# Revit family: 11
name_source: partatom
category: Lighting Fixtures
revit_build: Autodesk Revit 2014 (Build: 20130308_1515(x64)
units: mm (PartAtom-declared; Revit-internal decimal feet)

## types (1)
- P500324-104
    Apparent Load = 60 VA
    Assembly Code = D5020200
    Color Filter = 16777215
    Connector Description = Lighting Connector
    Default Elevation = 48 "
    Description = Embrace stylish simplicity with the Hinton Collection 1-Light Polished Nickel Clear Seeded Glass Vintage Hanging Pendant Light. The circular ceiling plate and industrial light base are coated in a crisp polished chrome finish. A light source glows from inside a clear seeded glass shade that provides effective task lighting wherever focused illumination is called upon.
    Dimming Lamp Color Temperature Shift = <None>
    Features = Application: Embrace stylish simplicity with the Hinton Collection 1-Light Polished Nickel Clear Seeded Glass Vintage Hanging Pendant Light is ideal for any foyer, dining room, kitchen, breakfast nook, entryway, living room, or stairway.
Styles: Perfect for farmhouse, transitional, and vintage electric style settings.
Finish: The circular ceiling plate and industrial light base are coated in a crisp polished chrome finish.
Materials: Constructed from steel to ensure a long product lifespan.
Glass/Shades: A light source glows from inside a clear seeded glass shade that provides effective task lighting wherever focused illumination is called upon.
Bulbs: For ideal illumination, use 1 medium base bulb that is sold separately (60w max - LED/CFL/incandescent). Compatible with dimmable bulbs.
Dimensions: Measures 12-inch diameter by 12-1/2-inch height.
Certifications: cULus damp location listed.
Pairs With: Pairs with a variety of Progress Lighting fixtures.
Warranty: Our 1-Year Limited Warranty guarantees your complete satisfaction with your purchase and includes professional after-sales customer service support.
    Fixture distribution = Direct
    Glass = Paint - Hubbell - White Texture
    Gold = Hubbell - Gold
    Height = 11 "
    Housing Material = Paint - Hubbell - Light Silver
    Lamp = LED or Medium Base
    Load Classification = Lighting
    Manufacturer = Progress Lighting
    Model = P500324-104
    Photometric Web File = generic.ies
    Power Factor = 1
    Product Documentation Link = https://hubbellcdn.com
    Product Link = https://www.hubbell.com
    Square = 12 "
    Tilt Angle = -90.00°
    URL = https://www.hubbell.com
    Voltage = 120 V
    Warranty = 1 year Warranty
    Wattage Comments = 60
    Watts = 60 W

## geometry (parser evidence)
native form markers: Sweep x4
no freeform markers — native parametric forms only
